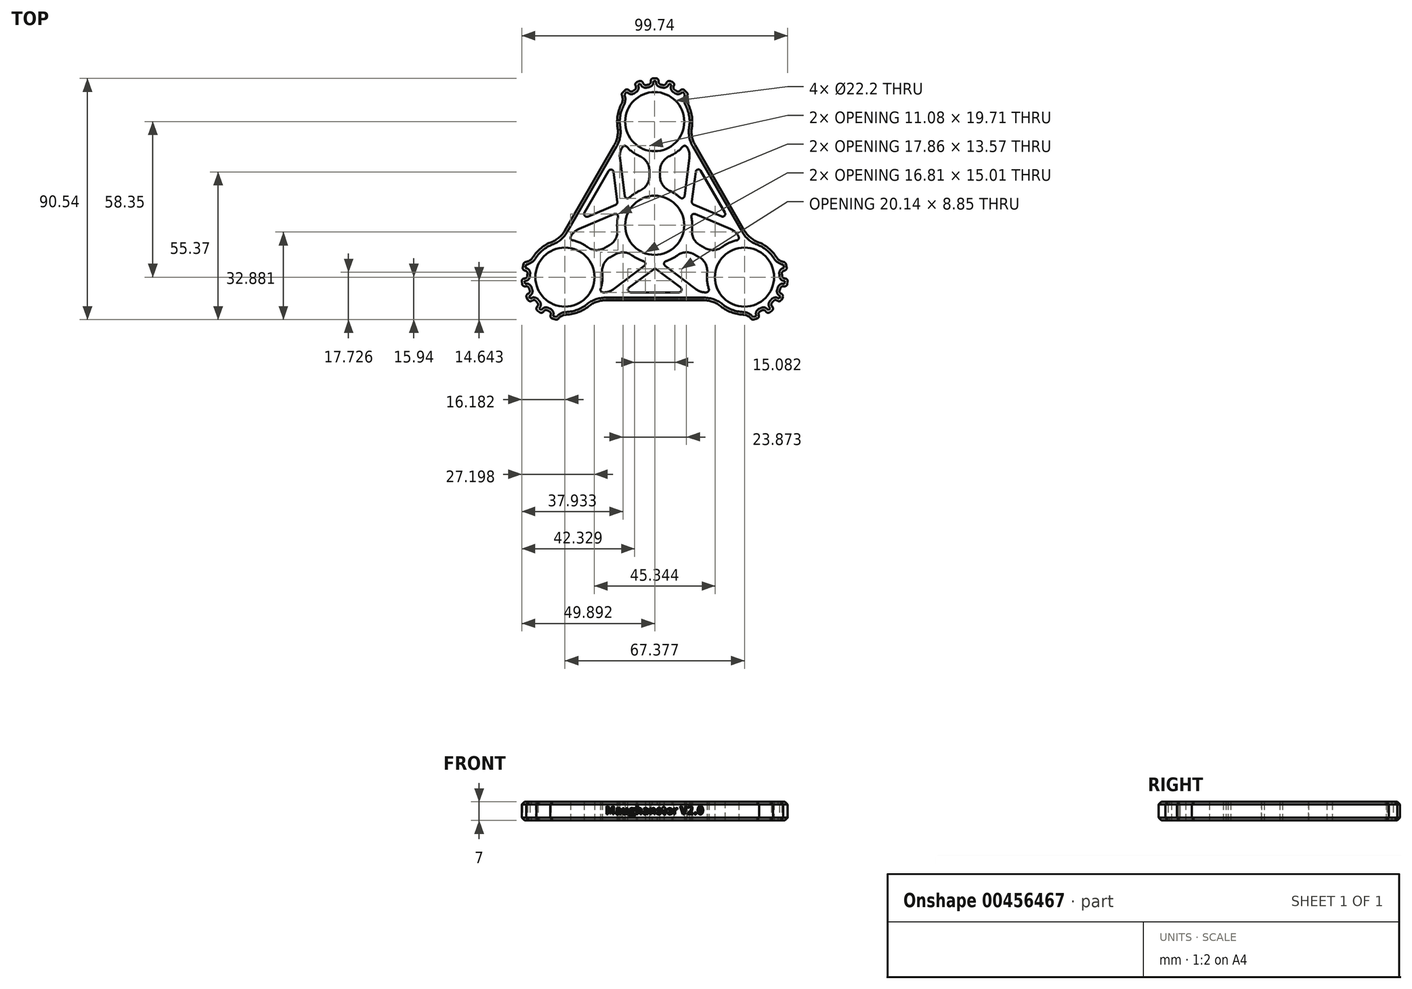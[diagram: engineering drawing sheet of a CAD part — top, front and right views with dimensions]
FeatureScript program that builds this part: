
annotation { "Feature Type Name" : "Feature", "Feature Type Description" : "" }
export const myFeature = defineFeature(function(context is Context, id is Id, definition is map)
    precondition{}
    {
        {
            var Q0;
            Q0=qCreatedBy(makeId("Top.planeOp"),FACE);
            var sketch = newSketch(context, id + "F0", { "sketchPlane" : qUnion([Q0])});
            skCircle(sketch, "E0", {"center": v(0, 0) * mm, "radius": 11.1 * mm});
            skArc(sketch, "E1.0", {"start": v(-2, 13.96) * mm, "mid": v(-6.94, 12.27) * mm, "end": v(-10.94, 8.9) * mm});
            skCircle(sketch, "E2", {"center": v(0, 38.9) * mm, "radius": 11.1 * mm});
            skArc(sketch, "E3.0", {"start": v(-10.97, 47.75) * mm, "mid": v(-13.94, 41) * mm, "end": v(-13.1, 33.66) * mm});
            skLineSegment(sketch, "E4", {"start": v(0, 11.1) * mm, "end": v(0, 27.8) * mm, "construction": true});
            skLineSegment(sketch, "E5.0", {"start": v(2, 13.96) * mm, "end": v(2, 24.94) * mm});
            skLineSegment(sketch, "E6.0", {"start": v(-2, 13.96) * mm, "end": v(-2, 24.94) * mm});
            skLineSegment(sketch, "E7", {"start": v(0, 53) * mm, "end": v(0, 55) * mm, "construction": true});
            skLineSegment(sketch, "E8.0", {"start": v(1.5, 52.92) * mm, "end": v(1.5, 55.15) * mm});
            skLineSegment(sketch, "E9.0", {"start": v(-1.5, 52.92) * mm, "end": v(-1.5, 55.15) * mm});
            skLineSegment(sketch, "E10", {"start": v(-1.5, 55.15) * mm, "end": v(1.5, 55.15) * mm});
            skLineSegment(sketch, "E11.1.0", {"start": v(4.83, 54.49) * mm, "end": v(7.6, 53.34) * mm});
            skLineSegment(sketch, "E11.1.1", {"start": v(3.98, 52.43) * mm, "end": v(4.83, 54.49) * mm});
            skLineSegment(sketch, "E11.1.2", {"start": v(6.75, 51.28) * mm, "end": v(7.6, 53.34) * mm});
            skLineSegment(sketch, "E11.2.0", {"start": v(10.43, 51.45) * mm, "end": v(12.55, 49.33) * mm});
            skLineSegment(sketch, "E11.2.1", {"start": v(8.85, 49.87) * mm, "end": v(10.43, 51.45) * mm});
            skLineSegment(sketch, "E11.2.2", {"start": v(10.97, 47.75) * mm, "end": v(12.55, 49.33) * mm});
            skLineSegment(sketch, "E11.anchor1", {"start": v(0, 38.9) * mm, "end": v(-1.5, 55.15) * mm, "construction": true});
            skLineSegment(sketch, "E11.anchor2", {"start": v(0, 38.9) * mm, "end": v(10.43, 51.45) * mm, "construction": true});
            skLineSegment(sketch, "E12.MirrorCS", {"start": v(-4.83, 54.49) * mm, "end": v(-7.6, 53.34) * mm});
            skLineSegment(sketch, "E13.MirrorCS", {"start": v(-3.98, 52.43) * mm, "end": v(-4.83, 54.49) * mm});
            skLineSegment(sketch, "E14.MirrorCS", {"start": v(-6.75, 51.28) * mm, "end": v(-7.6, 53.34) * mm});
            skLineSegment(sketch, "E15.MirrorCS", {"start": v(-8.85, 49.87) * mm, "end": v(-10.43, 51.45) * mm});
            skLineSegment(sketch, "E16.MirrorCS", {"start": v(-10.43, 51.45) * mm, "end": v(-12.55, 49.33) * mm});
            skLineSegment(sketch, "E17.MirrorCS", {"start": v(-10.97, 47.75) * mm, "end": v(-12.55, 49.33) * mm});
            skArc(sketch, "E18.trimOffspring", {"start": v(-6.75, 51.28) * mm, "mid": v(-7.83, 50.62) * mm, "end": v(-8.85, 49.87) * mm});
            skArc(sketch, "E19.trimOffspring", {"start": v(-1.3, 52.94) * mm, "mid": v(-2.65, 52.75) * mm, "end": v(-3.98, 52.43) * mm});
            skArc(sketch, "E20.trimOffspring", {"start": v(3.98, 52.43) * mm, "mid": v(2.75, 52.73) * mm, "end": v(1.5, 52.92) * mm});
            skArc(sketch, "E21.trimOffspring", {"start": v(9.01, 49.74) * mm, "mid": v(7.92, 50.57) * mm, "end": v(6.75, 51.28) * mm});
            skArc(sketch, "E22.trimOffspring", {"start": v(2, 24.94) * mm, "mid": v(7.27, 26.82) * mm, "end": v(11.4, 30.6) * mm});
            skLineSegment(sketch, "E23.1.0", {"start": v(-33.69, -19.45) * mm, "end": v(-47.01, -28.87) * mm, "construction": true});
            skPoint(sketch, "E23.1.1", {"position": v(-33.69, -19.45) * mm});
            skCircle(sketch, "E23.1.2", {"center": v(-33.69, -19.45) * mm, "radius": 11.1 * mm});
            skLineSegment(sketch, "E23.1.3", {"start": v(-9.61, -5.55) * mm, "end": v(-24.08, -13.9) * mm, "construction": true});
            skArc(sketch, "E23.1.4", {"start": v(-35.87, -33.38) * mm, "mid": v(-28.53, -32.57) * mm, "end": v(-22.6, -28.17) * mm});
            skLineSegment(sketch, "E23.1.5", {"start": v(-13.09, -5.25) * mm, "end": v(-22.6, -10.74) * mm});
            skLineSegment(sketch, "E23.1.6", {"start": v(-11.09, -8.71) * mm, "end": v(-20.6, -14.2) * mm});
            skLineSegment(sketch, "E23.1.7", {"start": v(-33.69, -19.45) * mm, "end": v(-49.77, -16.7) * mm, "construction": true});
            skArc(sketch, "E23.1.8", {"start": v(-22.6, -10.74) * mm, "mid": v(-26.86, -7.11) * mm, "end": v(-32.2, -5.43) * mm});
            skLineSegment(sketch, "E23.1.9", {"start": v(-41.03, -31.49) * mm, "end": v(-42.4, -33.26) * mm});
            skLineSegment(sketch, "E23.1.10", {"start": v(-35.87, -33.38) * mm, "end": v(-36.45, -35.53) * mm});
            skLineSegment(sketch, "E23.1.11", {"start": v(-49.77, -16.7) * mm, "end": v(-49, -13.8) * mm});
            skLineSegment(sketch, "E23.1.12", {"start": v(-47.78, -19.8) * mm, "end": v(-50, -20.08) * mm});
            skArc(sketch, "E23.1.13", {"start": v(-47.59, -17.07) * mm, "mid": v(-47.75, -18.43) * mm, "end": v(-47.78, -19.8) * mm});
            skLineSegment(sketch, "E23.1.14", {"start": v(-44.77, -31.43) * mm, "end": v(-42.4, -33.26) * mm});
            skLineSegment(sketch, "E23.1.15", {"start": v(-45.9, -26.5) * mm, "end": v(-47.63, -27.5) * mm, "construction": true});
            skLineSegment(sketch, "E23.1.16", {"start": v(-46.58, -25.16) * mm, "end": v(-48.51, -26.28) * mm});
            skLineSegment(sketch, "E23.1.17", {"start": v(-47.01, -28.87) * mm, "end": v(-48.51, -26.28) * mm});
            skLineSegment(sketch, "E23.1.18", {"start": v(-45.08, -27.76) * mm, "end": v(-47.01, -28.87) * mm});
            skLineSegment(sketch, "E23.1.19", {"start": v(-49.6, -23.06) * mm, "end": v(-50, -20.08) * mm});
            skLineSegment(sketch, "E23.1.20", {"start": v(-47.4, -22.77) * mm, "end": v(-49.6, -23.06) * mm});
            skArc(sketch, "E23.1.21", {"start": v(-47.4, -22.77) * mm, "mid": v(-47.04, -23.98) * mm, "end": v(-46.58, -25.16) * mm});
            skArc(sketch, "E23.1.22", {"start": v(-41.03, -31.49) * mm, "mid": v(-39.92, -32.1) * mm, "end": v(-38.77, -32.6) * mm});
            skLineSegment(sketch, "E23.1.23", {"start": v(-39.34, -34.76) * mm, "end": v(-36.45, -35.53) * mm});
            skLineSegment(sketch, "E23.1.24", {"start": v(-43.41, -29.66) * mm, "end": v(-44.77, -31.43) * mm});
            skLineSegment(sketch, "E23.1.25", {"start": v(-46.84, -14.37) * mm, "end": v(-49, -13.8) * mm});
            skArc(sketch, "E23.1.26", {"start": v(-45.2, -27.6) * mm, "mid": v(-44.36, -28.67) * mm, "end": v(-43.41, -29.66) * mm});
            skLineSegment(sketch, "E23.1.27", {"start": v(-38.77, -32.6) * mm, "end": v(-39.34, -34.76) * mm});
            skLineSegment(sketch, "E23.1.28", {"start": v(-47.62, -17.27) * mm, "end": v(-49.77, -16.7) * mm});
            skLineSegment(sketch, "E23.2.0", {"start": v(33.69, -19.45) * mm, "end": v(48.51, -26.28) * mm, "construction": true});
            skPoint(sketch, "E23.2.1", {"position": v(33.69, -19.45) * mm});
            skCircle(sketch, "E23.2.2", {"center": v(33.69, -19.45) * mm, "radius": 11.1 * mm});
            skLineSegment(sketch, "E23.2.3", {"start": v(9.61, -5.55) * mm, "end": v(24.08, -13.9) * mm, "construction": true});
            skArc(sketch, "E23.2.4", {"start": v(46.84, -14.37) * mm, "mid": v(42.48, -8.42) * mm, "end": v(35.7, -5.5) * mm});
            skLineSegment(sketch, "E23.2.5", {"start": v(11.09, -8.71) * mm, "end": v(20.6, -14.2) * mm});
            skLineSegment(sketch, "E23.2.6", {"start": v(13.09, -5.25) * mm, "end": v(22.6, -10.74) * mm});
            skLineSegment(sketch, "E23.2.7", {"start": v(33.69, -19.45) * mm, "end": v(39.34, -34.76) * mm, "construction": true});
            skArc(sketch, "E23.2.8", {"start": v(20.6, -14.2) * mm, "mid": v(19.6, -19.7) * mm, "end": v(20.8, -25.17) * mm});
            skLineSegment(sketch, "E23.2.9", {"start": v(47.78, -19.8) * mm, "end": v(50, -20.08) * mm});
            skLineSegment(sketch, "E23.2.10", {"start": v(46.84, -14.37) * mm, "end": v(49, -13.8) * mm});
            skLineSegment(sketch, "E23.2.11", {"start": v(39.34, -34.76) * mm, "end": v(36.45, -35.53) * mm});
            skLineSegment(sketch, "E23.2.12", {"start": v(41.03, -31.49) * mm, "end": v(42.4, -33.26) * mm});
            skArc(sketch, "E23.2.13", {"start": v(38.57, -32.68) * mm, "mid": v(39.83, -32.14) * mm, "end": v(41.03, -31.49) * mm});
            skLineSegment(sketch, "E23.2.14", {"start": v(49.6, -23.06) * mm, "end": v(50, -20.08) * mm});
            skLineSegment(sketch, "E23.2.15", {"start": v(45.9, -26.5) * mm, "end": v(47.63, -27.5) * mm, "construction": true});
            skLineSegment(sketch, "E23.2.16", {"start": v(45.08, -27.76) * mm, "end": v(47.01, -28.87) * mm});
            skLineSegment(sketch, "E23.2.17", {"start": v(48.51, -26.28) * mm, "end": v(47.01, -28.87) * mm});
            skLineSegment(sketch, "E23.2.18", {"start": v(46.58, -25.16) * mm, "end": v(48.51, -26.28) * mm});
            skLineSegment(sketch, "E23.2.19", {"start": v(44.77, -31.43) * mm, "end": v(42.4, -33.26) * mm});
            skLineSegment(sketch, "E23.2.20", {"start": v(43.41, -29.66) * mm, "end": v(44.77, -31.43) * mm});
            skArc(sketch, "E23.2.21", {"start": v(43.41, -29.66) * mm, "mid": v(44.29, -28.75) * mm, "end": v(45.08, -27.76) * mm});
            skArc(sketch, "E23.2.22", {"start": v(47.78, -19.8) * mm, "mid": v(47.76, -18.53) * mm, "end": v(47.62, -17.27) * mm});
            skLineSegment(sketch, "E23.2.23", {"start": v(49.77, -16.7) * mm, "end": v(49, -13.8) * mm});
            skLineSegment(sketch, "E23.2.24", {"start": v(47.4, -22.77) * mm, "end": v(49.6, -23.06) * mm});
            skLineSegment(sketch, "E23.2.25", {"start": v(35.87, -33.38) * mm, "end": v(36.45, -35.53) * mm});
            skArc(sketch, "E23.2.26", {"start": v(46.5, -25.35) * mm, "mid": v(47, -24.08) * mm, "end": v(47.4, -22.77) * mm});
            skLineSegment(sketch, "E23.2.27", {"start": v(47.62, -17.27) * mm, "end": v(49.77, -16.7) * mm});
            skLineSegment(sketch, "E23.2.28", {"start": v(38.77, -32.6) * mm, "end": v(39.34, -34.76) * mm});
            skArc(sketch, "E24.trimOffspring", {"start": v(13.09, -5.25) * mm, "mid": v(14.1, -0.12) * mm, "end": v(13.18, 5.02) * mm});
            skArc(sketch, "E25.trimOffspring", {"start": v(-11.09, -8.71) * mm, "mid": v(-7.15, -12.15) * mm, "end": v(-2.24, -13.92) * mm});
            skLineSegment(sketch, "E26", {"start": v(-13.1, 33.66) * mm, "end": v(-35.7, -5.5) * mm});
            skLineSegment(sketch, "E27.0", {"start": v(-11.4, 30.6) * mm, "end": v(-13.3, 27.31) * mm});
            skArc(sketch, "E28.trimOffspring", {"start": v(-11.4, 30.6) * mm, "mid": v(-7.27, 26.82) * mm, "end": v(-2, 24.94) * mm});
            skArc(sketch, "E29.trimOffspring", {"start": v(-35.7, -5.5) * mm, "mid": v(-42.48, -8.42) * mm, "end": v(-46.84, -14.37) * mm});
            skLineSegment(sketch, "E30", {"start": v(-12.21, 7.05) * mm, "end": v(-29.06, 0) * mm, "construction": true});
            skLineSegment(sketch, "E31", {"start": v(-12.21, 7.05) * mm, "end": v(-21.8, 12.59) * mm, "construction": true});
            skLineSegment(sketch, "E32.0", {"start": v(-13.97, 7.94) * mm, "end": v(-27.83, 2.14) * mm});
            skLineSegment(sketch, "E33.0", {"start": v(-13.18, 5.02) * mm, "end": v(-30.3, -2.14) * mm});
            skLineSegment(sketch, "E34.trimOffspring", {"start": v(-30.3, -2.14) * mm, "end": v(-32.2, -5.43) * mm});
            skArc(sketch, "E35.trimOffspring", {"start": v(-13.18, 5.02) * mm, "mid": v(-14.1, -0.12) * mm, "end": v(-13.09, -5.25) * mm});
            skLineSegment(sketch, "E36.MirrorCS", {"start": v(-10.94, 8.9) * mm, "end": v(-13.3, 27.31) * mm});
            skLineSegment(sketch, "E37.trimOffspring", {"start": v(-15.77, 23.03) * mm, "end": v(-27.83, 2.14) * mm});
            skPoint(sketch, "E38.orphan", {"position": v(-10.53, 9.38) * mm});
            skLineSegment(sketch, "E39.trimOffspring", {"start": v(-13.97, 7.94) * mm, "end": v(-15.77, 23.03) * mm});
            skPoint(sketch, "E40.MirrorCS.start.orphan", {"position": v(-13.39, 4.43) * mm});
            skLineSegment(sketch, "E41.1.0", {"start": v(-22.6, -28.17) * mm, "end": v(22.6, -28.17) * mm});
            skLineSegment(sketch, "E41.1.1", {"start": v(0.11, -16.07) * mm, "end": v(-12.06, -25.17) * mm});
            skLineSegment(sketch, "E41.1.2", {"start": v(0, -14.1) * mm, "end": v(0, -25.17) * mm, "construction": true});
            skLineSegment(sketch, "E41.1.3", {"start": v(-12.06, -25.17) * mm, "end": v(12.06, -25.17) * mm});
            skLineSegment(sketch, "E41.1.4", {"start": v(-2.24, -13.92) * mm, "end": v(-17, -25.17) * mm});
            skLineSegment(sketch, "E41.1.5", {"start": v(17, -25.17) * mm, "end": v(20.8, -25.17) * mm});
            skLineSegment(sketch, "E41.1.6", {"start": v(2.24, -13.92) * mm, "end": v(17, -25.17) * mm});
            skLineSegment(sketch, "E41.1.7", {"start": v(0.11, -16.07) * mm, "end": v(12.06, -25.17) * mm});
            skLineSegment(sketch, "E41.1.8", {"start": v(0, -14.1) * mm, "end": v(14.53, -25.17) * mm, "construction": true});
            skLineSegment(sketch, "E41.1.9", {"start": v(-20.8, -25.17) * mm, "end": v(-17, -25.17) * mm});
            skLineSegment(sketch, "E41.2.0", {"start": v(35.7, -5.5) * mm, "end": v(13.1, 33.66) * mm});
            skLineSegment(sketch, "E41.2.1", {"start": v(13.86, 8.13) * mm, "end": v(27.83, 2.14) * mm});
            skLineSegment(sketch, "E41.2.2", {"start": v(12.21, 7.05) * mm, "end": v(21.8, 12.59) * mm, "construction": true});
            skLineSegment(sketch, "E41.2.3", {"start": v(27.83, 2.14) * mm, "end": v(15.77, 23.03) * mm});
            skLineSegment(sketch, "E41.2.4", {"start": v(13.18, 5.02) * mm, "end": v(30.3, -2.14) * mm});
            skLineSegment(sketch, "E41.2.5", {"start": v(13.3, 27.31) * mm, "end": v(11.4, 30.6) * mm});
            skLineSegment(sketch, "E41.2.6", {"start": v(10.94, 8.9) * mm, "end": v(13.3, 27.31) * mm});
            skLineSegment(sketch, "E41.2.7", {"start": v(13.86, 8.13) * mm, "end": v(15.77, 23.03) * mm});
            skLineSegment(sketch, "E41.2.8", {"start": v(12.21, 7.05) * mm, "end": v(14.53, 25.17) * mm, "construction": true});
            skLineSegment(sketch, "E41.2.9", {"start": v(32.2, -5.43) * mm, "end": v(30.3, -2.14) * mm});
            skArc(sketch, "E42.trimOffspring", {"start": v(13.1, 33.66) * mm, "mid": v(13.94, 41) * mm, "end": v(10.97, 47.75) * mm});
            skArc(sketch, "E43.trimOffspring", {"start": v(32.2, -5.43) * mm, "mid": v(26.86, -7.11) * mm, "end": v(22.6, -10.74) * mm});
            skArc(sketch, "E44.trimOffspring", {"start": v(10.94, 8.9) * mm, "mid": v(6.94, 12.27) * mm, "end": v(2, 13.96) * mm});
            skArc(sketch, "E45.trimOffspring", {"start": v(2.24, -13.92) * mm, "mid": v(7.15, -12.15) * mm, "end": v(11.09, -8.71) * mm});
            skArc(sketch, "E46.trimOffspring", {"start": v(22.6, -28.17) * mm, "mid": v(28.53, -32.57) * mm, "end": v(35.87, -33.38) * mm});
            skArc(sketch, "E47.trimOffspring", {"start": v(-20.8, -25.17) * mm, "mid": v(-19.6, -19.7) * mm, "end": v(-20.6, -14.2) * mm});
            skSolve(sketch);
        }
        {
            var Q0;
            Q0 = qSketchRegion(id + "F0", true);
            extrude(context, id + "F1", {"entities" : qUnion([Q0]), "depth" : 7 * mm});
        }
        {
            var Q0;
            Q0=makeQuery(id+"F1.opExtrude","SWEPT_EDGE",EDGE,{"disambiguationData":[OSD([sQuery(id+"F0.wireOp",EDGE,"E1.0"),sQuery(id+"F0.wireOp",EDGE,"E6.0")])]});
            var Q1;
            Q1=makeQuery(id+"F1.opExtrude","SWEPT_EDGE",EDGE,{"disambiguationData":[OSD([sQuery(id+"F0.wireOp",EDGE,"E5.0"),sQuery(id+"F0.wireOp",EDGE,"E44.trimOffspring")])]});
            var Q2;
            Q2=makeQuery(id+"F1.opExtrude","SWEPT_EDGE",EDGE,{"disambiguationData":[OSD([sQuery(id+"F0.wireOp",EDGE,"E5.0"),sQuery(id+"F0.wireOp",EDGE,"E22.trimOffspring")])]});
            var Q3;
            Q3=makeQuery(id+"F1.opExtrude","SWEPT_EDGE",EDGE,{"disambiguationData":[OSD([sQuery(id+"F0.wireOp",EDGE,"E6.0"),sQuery(id+"F0.wireOp",EDGE,"E28.trimOffspring")])]});
            var Q4;
            Q4=makeQuery(id+"F1.opExtrude","SWEPT_EDGE",EDGE,{"disambiguationData":[OSD([sQuery(id+"F0.wireOp",EDGE,"E23.1.5"),sQuery(id+"F0.wireOp",EDGE,"E35.trimOffspring")])]});
            var Q5;
            Q5=makeQuery(id+"F1.opExtrude","SWEPT_EDGE",EDGE,{"disambiguationData":[OSD([sQuery(id+"F0.wireOp",EDGE,"E23.2.5"),sQuery(id+"F0.wireOp",EDGE,"E23.2.8")])]});
            var Q6;
            Q6=makeQuery(id+"F1.opExtrude","SWEPT_EDGE",EDGE,{"disambiguationData":[OSD([sQuery(id+"F0.wireOp",EDGE,"E23.1.6"),sQuery(id+"F0.wireOp",EDGE,"E47.trimOffspring")])]});
            var Q7;
            Q7=makeQuery(id+"F1.opExtrude","SWEPT_EDGE",EDGE,{"disambiguationData":[OSD([sQuery(id+"F0.wireOp",EDGE,"E23.1.6"),sQuery(id+"F0.wireOp",EDGE,"E25.trimOffspring")])]});
            var Q8;
            Q8=makeQuery(id+"F1.opExtrude","SWEPT_EDGE",EDGE,{"disambiguationData":[OSD([sQuery(id+"F0.wireOp",EDGE,"E23.1.5"),sQuery(id+"F0.wireOp",EDGE,"E23.1.8")])]});
            var Q9;
            Q9=makeQuery(id+"F1.opExtrude","SWEPT_EDGE",EDGE,{"disambiguationData":[OSD([sQuery(id+"F0.wireOp",EDGE,"E23.2.6"),sQuery(id+"F0.wireOp",EDGE,"E43.trimOffspring")])]});
            var Q10;
            Q10=makeQuery(id+"F1.opExtrude","SWEPT_EDGE",EDGE,{"disambiguationData":[OSD([sQuery(id+"F0.wireOp",EDGE,"E23.2.5"),sQuery(id+"F0.wireOp",EDGE,"E45.trimOffspring")])]});
            var Q11;
            Q11=makeQuery(id+"F1.opExtrude","SWEPT_EDGE",EDGE,{"disambiguationData":[OSD([sQuery(id+"F0.wireOp",EDGE,"E23.2.6"),sQuery(id+"F0.wireOp",EDGE,"E24.trimOffspring")])]});
            var Q12;
            Q12=makeQuery(id+"F1.opExtrude","SWEPT_EDGE",EDGE,{"disambiguationData":[OSD([sQuery(id+"F0.wireOp",EDGE,"E33.0"),sQuery(id+"F0.wireOp",EDGE,"E34.trimOffspring")])]});
            var Q13;
            Q13=makeQuery(id+"F1.opExtrude","SWEPT_EDGE",EDGE,{"disambiguationData":[OSD([sQuery(id+"F0.wireOp",EDGE,"E41.1.4"),sQuery(id+"F0.wireOp",EDGE,"E41.1.9")])]});
            var Q14;
            Q14=makeQuery(id+"F1.opExtrude","SWEPT_EDGE",EDGE,{"disambiguationData":[OSD([sQuery(id+"F0.wireOp",EDGE,"E41.1.5"),sQuery(id+"F0.wireOp",EDGE,"E41.1.6")])]});
            var Q15;
            Q15=makeQuery(id+"F1.opExtrude","SWEPT_EDGE",EDGE,{"disambiguationData":[OSD([sQuery(id+"F0.wireOp",EDGE,"E41.2.5"),sQuery(id+"F0.wireOp",EDGE,"E41.2.6")])]});
            var Q16;
            Q16=makeQuery(id+"F1.opExtrude","SWEPT_EDGE",EDGE,{"disambiguationData":[OSD([sQuery(id+"F0.wireOp",EDGE,"E41.2.4"),sQuery(id+"F0.wireOp",EDGE,"E41.2.9")])]});
            var Q17;
            Q17=makeQuery(id+"F1.opExtrude","SWEPT_EDGE",EDGE,{"disambiguationData":[OSD([sQuery(id+"F0.wireOp",EDGE,"E27.0"),sQuery(id+"F0.wireOp",EDGE,"E36.MirrorCS")])]});
            fillet(context, id + "F2", {"entities" : qUnion([Q0, Q1, Q2, Q3, Q4, Q5, Q6, Q7, Q8, Q9, Q10, Q11, Q12, Q13, Q14, Q15, Q16, Q17]), "radius" : 6 * mm, "tangentPropagation" : true, "allowEdgeOverflow" : false});
        }
        {
            var Q0;
            Q0=makeQuery(id+"F1.opExtrude","SWEPT_EDGE",EDGE,{"disambiguationData":[OSD([sQuery(id+"F0.wireOp",EDGE,"E1.0"),sQuery(id+"F0.wireOp",EDGE,"E36.MirrorCS")])]});
            var Q1;
            Q1=makeQuery(id+"F1.opExtrude","SWEPT_EDGE",EDGE,{"disambiguationData":[OSD([sQuery(id+"F0.wireOp",EDGE,"E33.0"),sQuery(id+"F0.wireOp",EDGE,"E35.trimOffspring")])]});
            var Q2;
            Q2=makeQuery(id+"F1.opExtrude","SWEPT_EDGE",EDGE,{"disambiguationData":[OSD([sQuery(id+"F0.wireOp",EDGE,"E25.trimOffspring"),sQuery(id+"F0.wireOp",EDGE,"E41.1.4")])]});
            var Q3;
            Q3=makeQuery(id+"F1.opExtrude","SWEPT_EDGE",EDGE,{"disambiguationData":[OSD([sQuery(id+"F0.wireOp",EDGE,"E41.1.6"),sQuery(id+"F0.wireOp",EDGE,"E45.trimOffspring")])]});
            var Q4;
            Q4=makeQuery(id+"F1.opExtrude","SWEPT_EDGE",EDGE,{"disambiguationData":[OSD([sQuery(id+"F0.wireOp",EDGE,"E24.trimOffspring"),sQuery(id+"F0.wireOp",EDGE,"E41.2.4")])]});
            var Q5;
            Q5=makeQuery(id+"F1.opExtrude","SWEPT_EDGE",EDGE,{"disambiguationData":[OSD([sQuery(id+"F0.wireOp",EDGE,"E41.2.6"),sQuery(id+"F0.wireOp",EDGE,"E44.trimOffspring")])]});
            var Q6;
            Q6=makeQuery(id+"F1.opExtrude","SWEPT_EDGE",EDGE,{"disambiguationData":[OSD([sQuery(id+"F0.wireOp",EDGE,"E41.2.9"),sQuery(id+"F0.wireOp",EDGE,"E43.trimOffspring")])]});
            var Q7;
            Q7=makeQuery(id+"F1.opExtrude","SWEPT_EDGE",EDGE,{"disambiguationData":[OSD([sQuery(id+"F0.wireOp",EDGE,"E23.2.8"),sQuery(id+"F0.wireOp",EDGE,"E41.1.5")])]});
            var Q8;
            Q8=makeQuery(id+"F1.opExtrude","SWEPT_EDGE",EDGE,{"disambiguationData":[OSD([sQuery(id+"F0.wireOp",EDGE,"E41.1.9"),sQuery(id+"F0.wireOp",EDGE,"E47.trimOffspring")])]});
            var Q9;
            Q9=makeQuery(id+"F1.opExtrude","SWEPT_EDGE",EDGE,{"disambiguationData":[OSD([sQuery(id+"F0.wireOp",EDGE,"E23.1.8"),sQuery(id+"F0.wireOp",EDGE,"E34.trimOffspring")])]});
            var Q10;
            Q10=makeQuery(id+"F1.opExtrude","SWEPT_EDGE",EDGE,{"disambiguationData":[OSD([sQuery(id+"F0.wireOp",EDGE,"E22.trimOffspring"),sQuery(id+"F0.wireOp",EDGE,"E41.2.5")])]});
            var Q11;
            Q11=makeQuery(id+"F1.opExtrude","SWEPT_EDGE",EDGE,{"disambiguationData":[OSD([sQuery(id+"F0.wireOp",EDGE,"E27.0"),sQuery(id+"F0.wireOp",EDGE,"E28.trimOffspring")])]});
            var Q12;
            Q12=makeQuery(id+"F1.opExtrude","SWEPT_EDGE",EDGE,{"disambiguationData":[OSD([sQuery(id+"F0.wireOp",EDGE,"E37.trimOffspring"),sQuery(id+"F0.wireOp",EDGE,"E39.trimOffspring")])]});
            var Q13;
            Q13=makeQuery(id+"F1.opExtrude","SWEPT_EDGE",EDGE,{"disambiguationData":[OSD([sQuery(id+"F0.wireOp",EDGE,"E32.0"),sQuery(id+"F0.wireOp",EDGE,"E37.trimOffspring")])]});
            var Q14;
            Q14=makeQuery(id+"F1.opExtrude","SWEPT_EDGE",EDGE,{"disambiguationData":[OSD([sQuery(id+"F0.wireOp",EDGE,"E41.2.1"),sQuery(id+"F0.wireOp",EDGE,"E41.2.3")])]});
            var Q15;
            Q15=makeQuery(id+"F1.opExtrude","SWEPT_EDGE",EDGE,{"disambiguationData":[OSD([sQuery(id+"F0.wireOp",EDGE,"E41.2.3"),sQuery(id+"F0.wireOp",EDGE,"E41.2.7")])]});
            var Q16;
            Q16=makeQuery(id+"F1.opExtrude","SWEPT_EDGE",EDGE,{"disambiguationData":[OSD([sQuery(id+"F0.wireOp",EDGE,"E41.1.3"),sQuery(id+"F0.wireOp",EDGE,"E41.1.7")])]});
            var Q17;
            Q17=makeQuery(id+"F1.opExtrude","SWEPT_EDGE",EDGE,{"disambiguationData":[OSD([sQuery(id+"F0.wireOp",EDGE,"E41.1.1"),sQuery(id+"F0.wireOp",EDGE,"E41.1.3")])]});
            var Q18;
            Q18=makeQuery(id+"F1.opExtrude","SWEPT_EDGE",EDGE,{"disambiguationData":[OSD([sQuery(id+"F0.wireOp",EDGE,"E32.0"),sQuery(id+"F0.wireOp",EDGE,"E39.trimOffspring")])]});
            var Q19;
            Q19=makeQuery(id+"F1.opExtrude","SWEPT_EDGE",EDGE,{"disambiguationData":[OSD([sQuery(id+"F0.wireOp",EDGE,"E41.1.1"),sQuery(id+"F0.wireOp",EDGE,"E41.1.7")])]});
            var Q20;
            Q20=makeQuery(id+"F1.opExtrude","SWEPT_EDGE",EDGE,{"disambiguationData":[OSD([sQuery(id+"F0.wireOp",EDGE,"E41.2.1"),sQuery(id+"F0.wireOp",EDGE,"E41.2.7")])]});
            fillet(context, id + "F3", {"entities" : qUnion([Q0, Q1, Q2, Q3, Q4, Q5, Q6, Q7, Q8, Q9, Q10, Q11, Q12, Q13, Q14, Q15, Q16, Q17, Q18, Q19, Q20]), "radius" : 1 * mm, "tangentPropagation" : true, "allowEdgeOverflow" : false});
        }
        {
            var Q0;
            Q0=makeQuery(id+"F1.opExtrude","SWEPT_EDGE",EDGE,{"disambiguationData":[OSD([sQuery(id+"F0.wireOp",EDGE,"E3.0"),sQuery(id+"F0.wireOp",EDGE,"E26")])]});
            var Q1;
            Q1=makeQuery(id+"F1.opExtrude","SWEPT_EDGE",EDGE,{"disambiguationData":[OSD([sQuery(id+"F0.wireOp",EDGE,"E41.2.0"),sQuery(id+"F0.wireOp",EDGE,"E42.trimOffspring")])]});
            var Q2;
            Q2=makeQuery(id+"F1.opExtrude","SWEPT_EDGE",EDGE,{"disambiguationData":[OSD([sQuery(id+"F0.wireOp",EDGE,"E26"),sQuery(id+"F0.wireOp",EDGE,"E29.trimOffspring")])]});
            var Q3;
            Q3=makeQuery(id+"F1.opExtrude","SWEPT_EDGE",EDGE,{"disambiguationData":[OSD([sQuery(id+"F0.wireOp",EDGE,"E23.1.4"),sQuery(id+"F0.wireOp",EDGE,"E41.1.0")])]});
            var Q4;
            Q4=makeQuery(id+"F1.opExtrude","SWEPT_EDGE",EDGE,{"disambiguationData":[OSD([sQuery(id+"F0.wireOp",EDGE,"E41.1.0"),sQuery(id+"F0.wireOp",EDGE,"E46.trimOffspring")])]});
            var Q5;
            Q5=makeQuery(id+"F1.opExtrude","SWEPT_EDGE",EDGE,{"disambiguationData":[OSD([sQuery(id+"F0.wireOp",EDGE,"E23.2.4"),sQuery(id+"F0.wireOp",EDGE,"E41.2.0")])]});
            fillet(context, id + "F4", {"entities" : qUnion([Q0, Q1, Q2, Q3, Q4, Q5]), "radius" : 10 * mm, "tangentPropagation" : true, "allowEdgeOverflow" : false});
        }
        {
            var Q0;
            Q0=makeQuery(id+"F1.opExtrude","SWEPT_EDGE",EDGE,{"disambiguationData":[OSD([sQuery(id+"F0.wireOp",EDGE,"E3.0"),sQuery(id+"F0.wireOp",EDGE,"E17.MirrorCS")])]});
            var Q1;
            Q1=makeQuery(id+"F1.opExtrude","SWEPT_EDGE",EDGE,{"disambiguationData":[OSD([sQuery(id+"F0.wireOp",EDGE,"E11.2.2"),sQuery(id+"F0.wireOp",EDGE,"E42.trimOffspring")])]});
            var Q2;
            Q2=makeQuery(id+"F1.opExtrude","SWEPT_EDGE",EDGE,{"disambiguationData":[OSD([sQuery(id+"F0.wireOp",EDGE,"E23.1.25"),sQuery(id+"F0.wireOp",EDGE,"E29.trimOffspring")])]});
            var Q3;
            Q3=makeQuery(id+"F1.opExtrude","SWEPT_EDGE",EDGE,{"disambiguationData":[OSD([sQuery(id+"F0.wireOp",EDGE,"E23.1.4"),sQuery(id+"F0.wireOp",EDGE,"E23.1.10")])]});
            var Q4;
            Q4=makeQuery(id+"F1.opExtrude","SWEPT_EDGE",EDGE,{"disambiguationData":[OSD([sQuery(id+"F0.wireOp",EDGE,"E23.2.25"),sQuery(id+"F0.wireOp",EDGE,"E46.trimOffspring")])]});
            var Q5;
            Q5=makeQuery(id+"F1.opExtrude","SWEPT_EDGE",EDGE,{"disambiguationData":[OSD([sQuery(id+"F0.wireOp",EDGE,"E23.2.4"),sQuery(id+"F0.wireOp",EDGE,"E23.2.10")])]});
            fillet(context, id + "F5", {"entities" : qUnion([Q0, Q1, Q2, Q3, Q4, Q5]), "radius" : 4 * mm, "tangentPropagation" : true, "allowEdgeOverflow" : false});
        }
        {
            var Q0;
            Q0=makeQuery(id+"F1.opExtrude","SWEPT_EDGE",EDGE,{"disambiguationData":[OSD([sQuery(id+"F0.wireOp",EDGE,"E15.MirrorCS"),sQuery(id+"F0.wireOp",EDGE,"E18.trimOffspring")])]});
            var Q1;
            Q1=makeQuery(id+"F1.opExtrude","SWEPT_EDGE",EDGE,{"disambiguationData":[OSD([sQuery(id+"F0.wireOp",EDGE,"E14.MirrorCS"),sQuery(id+"F0.wireOp",EDGE,"E18.trimOffspring")])]});
            var Q2;
            Q2=makeQuery(id+"F1.opExtrude","SWEPT_EDGE",EDGE,{"disambiguationData":[OSD([sQuery(id+"F0.wireOp",EDGE,"E13.MirrorCS"),sQuery(id+"F0.wireOp",EDGE,"E19.trimOffspring")])]});
            var Q3;
            Q3=makeQuery(id+"F1.opExtrude","SWEPT_EDGE",EDGE,{"disambiguationData":[OSD([sQuery(id+"F0.wireOp",EDGE,"E9.0"),sQuery(id+"F0.wireOp",EDGE,"E19.trimOffspring")])]});
            var Q4;
            Q4=makeQuery(id+"F1.opExtrude","SWEPT_EDGE",EDGE,{"disambiguationData":[OSD([sQuery(id+"F0.wireOp",EDGE,"E8.0"),sQuery(id+"F0.wireOp",EDGE,"E20.trimOffspring")])]});
            var Q5;
            Q5=makeQuery(id+"F1.opExtrude","SWEPT_EDGE",EDGE,{"disambiguationData":[OSD([sQuery(id+"F0.wireOp",EDGE,"E11.1.2"),sQuery(id+"F0.wireOp",EDGE,"E21.trimOffspring")])]});
            var Q6;
            Q6=makeQuery(id+"F1.opExtrude","SWEPT_EDGE",EDGE,{"disambiguationData":[OSD([sQuery(id+"F0.wireOp",EDGE,"E11.1.1"),sQuery(id+"F0.wireOp",EDGE,"E20.trimOffspring")])]});
            var Q7;
            Q7=makeQuery(id+"F1.opExtrude","SWEPT_EDGE",EDGE,{"disambiguationData":[OSD([sQuery(id+"F0.wireOp",EDGE,"E11.2.1"),sQuery(id+"F0.wireOp",EDGE,"E21.trimOffspring")])]});
            var Q8;
            Q8=makeQuery(id+"F1.opExtrude","SWEPT_EDGE",EDGE,{"disambiguationData":[OSD([sQuery(id+"F0.wireOp",EDGE,"E23.1.13"),sQuery(id+"F0.wireOp",EDGE,"E23.1.28")])]});
            var Q9;
            Q9=makeQuery(id+"F1.opExtrude","SWEPT_EDGE",EDGE,{"disambiguationData":[OSD([sQuery(id+"F0.wireOp",EDGE,"E23.1.20"),sQuery(id+"F0.wireOp",EDGE,"E23.1.21")])]});
            var Q10;
            Q10=makeQuery(id+"F1.opExtrude","SWEPT_EDGE",EDGE,{"disambiguationData":[OSD([sQuery(id+"F0.wireOp",EDGE,"E23.1.9"),sQuery(id+"F0.wireOp",EDGE,"E23.1.22")])]});
            var Q11;
            Q11=makeQuery(id+"F1.opExtrude","SWEPT_EDGE",EDGE,{"disambiguationData":[OSD([sQuery(id+"F0.wireOp",EDGE,"E23.1.18"),sQuery(id+"F0.wireOp",EDGE,"E23.1.26")])]});
            var Q12;
            Q12=makeQuery(id+"F1.opExtrude","SWEPT_EDGE",EDGE,{"disambiguationData":[OSD([sQuery(id+"F0.wireOp",EDGE,"E23.1.12"),sQuery(id+"F0.wireOp",EDGE,"E23.1.13")])]});
            var Q13;
            Q13=makeQuery(id+"F1.opExtrude","SWEPT_EDGE",EDGE,{"disambiguationData":[OSD([sQuery(id+"F0.wireOp",EDGE,"E23.1.16"),sQuery(id+"F0.wireOp",EDGE,"E23.1.21")])]});
            var Q14;
            Q14=makeQuery(id+"F1.opExtrude","SWEPT_EDGE",EDGE,{"disambiguationData":[OSD([sQuery(id+"F0.wireOp",EDGE,"E23.1.24"),sQuery(id+"F0.wireOp",EDGE,"E23.1.26")])]});
            var Q15;
            Q15=makeQuery(id+"F1.opExtrude","SWEPT_EDGE",EDGE,{"disambiguationData":[OSD([sQuery(id+"F0.wireOp",EDGE,"E23.1.22"),sQuery(id+"F0.wireOp",EDGE,"E23.1.27")])]});
            var Q16;
            Q16=makeQuery(id+"F1.opExtrude","SWEPT_EDGE",EDGE,{"disambiguationData":[OSD([sQuery(id+"F0.wireOp",EDGE,"E23.2.22"),sQuery(id+"F0.wireOp",EDGE,"E23.2.27")])]});
            var Q17;
            Q17=makeQuery(id+"F1.opExtrude","SWEPT_EDGE",EDGE,{"disambiguationData":[OSD([sQuery(id+"F0.wireOp",EDGE,"E23.2.24"),sQuery(id+"F0.wireOp",EDGE,"E23.2.26")])]});
            var Q18;
            Q18=makeQuery(id+"F1.opExtrude","SWEPT_EDGE",EDGE,{"disambiguationData":[OSD([sQuery(id+"F0.wireOp",EDGE,"E23.2.16"),sQuery(id+"F0.wireOp",EDGE,"E23.2.21")])]});
            var Q19;
            Q19=makeQuery(id+"F1.opExtrude","SWEPT_EDGE",EDGE,{"disambiguationData":[OSD([sQuery(id+"F0.wireOp",EDGE,"E23.2.12"),sQuery(id+"F0.wireOp",EDGE,"E23.2.13")])]});
            var Q20;
            Q20=makeQuery(id+"F1.opExtrude","SWEPT_EDGE",EDGE,{"disambiguationData":[OSD([sQuery(id+"F0.wireOp",EDGE,"E23.2.13"),sQuery(id+"F0.wireOp",EDGE,"E23.2.28")])]});
            var Q21;
            Q21=makeQuery(id+"F1.opExtrude","SWEPT_EDGE",EDGE,{"disambiguationData":[OSD([sQuery(id+"F0.wireOp",EDGE,"E23.2.20"),sQuery(id+"F0.wireOp",EDGE,"E23.2.21")])]});
            var Q22;
            Q22=makeQuery(id+"F1.opExtrude","SWEPT_EDGE",EDGE,{"disambiguationData":[OSD([sQuery(id+"F0.wireOp",EDGE,"E23.2.18"),sQuery(id+"F0.wireOp",EDGE,"E23.2.26")])]});
            var Q23;
            Q23=makeQuery(id+"F1.opExtrude","SWEPT_EDGE",EDGE,{"disambiguationData":[OSD([sQuery(id+"F0.wireOp",EDGE,"E23.2.9"),sQuery(id+"F0.wireOp",EDGE,"E23.2.22")])]});
            fillet(context, id + "F6", {"entities" : qUnion([Q0, Q1, Q2, Q3, Q4, Q5, Q6, Q7, Q8, Q9, Q10, Q11, Q12, Q13, Q14, Q15, Q16, Q17, Q18, Q19, Q20, Q21, Q22, Q23]), "radius" : 1 * mm, "tangentPropagation" : true, "allowEdgeOverflow" : false});
        }
        {
            var Q0;
            Q0=makeQuery(id+"F1.opExtrude","SWEPT_EDGE",EDGE,{"disambiguationData":[OSD([sQuery(id+"F0.wireOp",EDGE,"E12.MirrorCS"),sQuery(id+"F0.wireOp",EDGE,"E14.MirrorCS")])]});
            var Q1;
            Q1=makeQuery(id+"F1.opExtrude","SWEPT_EDGE",EDGE,{"disambiguationData":[OSD([sQuery(id+"F0.wireOp",EDGE,"E12.MirrorCS"),sQuery(id+"F0.wireOp",EDGE,"E13.MirrorCS")])]});
            var Q2;
            Q2=makeQuery(id+"F5.opFillet","BLEND_EDGE",EDGE,{"blendedFrom":[makeQuery(id+"F1.opExtrude","SWEPT_EDGE",EDGE,{"disambiguationData":[OSD([sQuery(id+"F0.wireOp",EDGE,"E3.0"),sQuery(id+"F0.wireOp",EDGE,"E17.MirrorCS")])]}),makeQuery(id+"F1.opExtrude","SWEPT_FACE",FACE,{"disambiguationData":[OSD([sQuery(id+"F0.wireOp",EDGE,"E16.MirrorCS")])]})],"blendedInto":[makeQuery(id+"F1.opExtrude","SWEPT_FACE",FACE,{"disambiguationData":[OSD([sQuery(id+"F0.wireOp",EDGE,"E16.MirrorCS")])]})]});
            var Q3;
            Q3=makeQuery(id+"F1.opExtrude","SWEPT_EDGE",EDGE,{"disambiguationData":[OSD([sQuery(id+"F0.wireOp",EDGE,"E15.MirrorCS"),sQuery(id+"F0.wireOp",EDGE,"E16.MirrorCS")])]});
            var Q4;
            Q4=makeQuery(id+"F1.opExtrude","SWEPT_EDGE",EDGE,{"disambiguationData":[OSD([sQuery(id+"F0.wireOp",EDGE,"E9.0"),sQuery(id+"F0.wireOp",EDGE,"E10")])]});
            var Q5;
            Q5=makeQuery(id+"F1.opExtrude","SWEPT_EDGE",EDGE,{"disambiguationData":[OSD([sQuery(id+"F0.wireOp",EDGE,"E8.0"),sQuery(id+"F0.wireOp",EDGE,"E10")])]});
            var Q6;
            Q6=makeQuery(id+"F1.opExtrude","SWEPT_EDGE",EDGE,{"disambiguationData":[OSD([sQuery(id+"F0.wireOp",EDGE,"E11.1.0"),sQuery(id+"F0.wireOp",EDGE,"E11.1.1")])]});
            var Q7;
            Q7=makeQuery(id+"F1.opExtrude","SWEPT_EDGE",EDGE,{"disambiguationData":[OSD([sQuery(id+"F0.wireOp",EDGE,"E11.1.0"),sQuery(id+"F0.wireOp",EDGE,"E11.1.2")])]});
            var Q8;
            Q8=makeQuery(id+"F1.opExtrude","SWEPT_EDGE",EDGE,{"disambiguationData":[OSD([sQuery(id+"F0.wireOp",EDGE,"E11.2.0"),sQuery(id+"F0.wireOp",EDGE,"E11.2.1")])]});
            var Q9;
            Q9=makeQuery(id+"F5.opFillet","BLEND_EDGE",EDGE,{"blendedFrom":[makeQuery(id+"F1.opExtrude","SWEPT_EDGE",EDGE,{"disambiguationData":[OSD([sQuery(id+"F0.wireOp",EDGE,"E11.2.2"),sQuery(id+"F0.wireOp",EDGE,"E42.trimOffspring")])]}),makeQuery(id+"F1.opExtrude","SWEPT_FACE",FACE,{"disambiguationData":[OSD([sQuery(id+"F0.wireOp",EDGE,"E11.2.0")])]})],"blendedInto":[makeQuery(id+"F1.opExtrude","SWEPT_FACE",FACE,{"disambiguationData":[OSD([sQuery(id+"F0.wireOp",EDGE,"E11.2.0")])]})]});
            var Q10;
            Q10=makeQuery(id+"F5.opFillet","BLEND_EDGE",EDGE,{"blendedFrom":[makeQuery(id+"F1.opExtrude","SWEPT_EDGE",EDGE,{"disambiguationData":[OSD([sQuery(id+"F0.wireOp",EDGE,"E23.1.25"),sQuery(id+"F0.wireOp",EDGE,"E29.trimOffspring")])]}),makeQuery(id+"F1.opExtrude","SWEPT_FACE",FACE,{"disambiguationData":[OSD([sQuery(id+"F0.wireOp",EDGE,"E23.1.11")])]})],"blendedInto":[makeQuery(id+"F1.opExtrude","SWEPT_FACE",FACE,{"disambiguationData":[OSD([sQuery(id+"F0.wireOp",EDGE,"E23.1.11")])]})]});
            var Q11;
            Q11=makeQuery(id+"F1.opExtrude","SWEPT_EDGE",EDGE,{"disambiguationData":[OSD([sQuery(id+"F0.wireOp",EDGE,"E23.1.11"),sQuery(id+"F0.wireOp",EDGE,"E23.1.28")])]});
            var Q12;
            Q12=makeQuery(id+"F1.opExtrude","SWEPT_EDGE",EDGE,{"disambiguationData":[OSD([sQuery(id+"F0.wireOp",EDGE,"E23.1.12"),sQuery(id+"F0.wireOp",EDGE,"E23.1.19")])]});
            var Q13;
            Q13=makeQuery(id+"F1.opExtrude","SWEPT_EDGE",EDGE,{"disambiguationData":[OSD([sQuery(id+"F0.wireOp",EDGE,"E23.1.19"),sQuery(id+"F0.wireOp",EDGE,"E23.1.20")])]});
            var Q14;
            Q14=makeQuery(id+"F1.opExtrude","SWEPT_EDGE",EDGE,{"disambiguationData":[OSD([sQuery(id+"F0.wireOp",EDGE,"E23.1.16"),sQuery(id+"F0.wireOp",EDGE,"E23.1.17")])]});
            var Q15;
            Q15=makeQuery(id+"F1.opExtrude","SWEPT_EDGE",EDGE,{"disambiguationData":[OSD([sQuery(id+"F0.wireOp",EDGE,"E23.1.17"),sQuery(id+"F0.wireOp",EDGE,"E23.1.18")])]});
            var Q16;
            Q16=makeQuery(id+"F1.opExtrude","SWEPT_EDGE",EDGE,{"disambiguationData":[OSD([sQuery(id+"F0.wireOp",EDGE,"E23.1.14"),sQuery(id+"F0.wireOp",EDGE,"E23.1.24")])]});
            var Q17;
            Q17=makeQuery(id+"F1.opExtrude","SWEPT_EDGE",EDGE,{"disambiguationData":[OSD([sQuery(id+"F0.wireOp",EDGE,"E23.1.9"),sQuery(id+"F0.wireOp",EDGE,"E23.1.14")])]});
            var Q18;
            Q18=makeQuery(id+"F1.opExtrude","SWEPT_EDGE",EDGE,{"disambiguationData":[OSD([sQuery(id+"F0.wireOp",EDGE,"E23.1.23"),sQuery(id+"F0.wireOp",EDGE,"E23.1.27")])]});
            var Q19;
            Q19=makeQuery(id+"F5.opFillet","BLEND_EDGE",EDGE,{"blendedFrom":[makeQuery(id+"F1.opExtrude","SWEPT_EDGE",EDGE,{"disambiguationData":[OSD([sQuery(id+"F0.wireOp",EDGE,"E23.1.4"),sQuery(id+"F0.wireOp",EDGE,"E23.1.10")])]}),makeQuery(id+"F1.opExtrude","SWEPT_FACE",FACE,{"disambiguationData":[OSD([sQuery(id+"F0.wireOp",EDGE,"E23.1.23")])]})],"blendedInto":[makeQuery(id+"F1.opExtrude","SWEPT_FACE",FACE,{"disambiguationData":[OSD([sQuery(id+"F0.wireOp",EDGE,"E23.1.23")])]})]});
            var Q20;
            Q20=makeQuery(id+"F5.opFillet","BLEND_EDGE",EDGE,{"blendedFrom":[makeQuery(id+"F1.opExtrude","SWEPT_EDGE",EDGE,{"disambiguationData":[OSD([sQuery(id+"F0.wireOp",EDGE,"E23.2.25"),sQuery(id+"F0.wireOp",EDGE,"E46.trimOffspring")])]}),makeQuery(id+"F1.opExtrude","SWEPT_FACE",FACE,{"disambiguationData":[OSD([sQuery(id+"F0.wireOp",EDGE,"E23.2.11")])]})],"blendedInto":[makeQuery(id+"F1.opExtrude","SWEPT_FACE",FACE,{"disambiguationData":[OSD([sQuery(id+"F0.wireOp",EDGE,"E23.2.11")])]})]});
            var Q21;
            Q21=makeQuery(id+"F1.opExtrude","SWEPT_EDGE",EDGE,{"disambiguationData":[OSD([sQuery(id+"F0.wireOp",EDGE,"E23.2.11"),sQuery(id+"F0.wireOp",EDGE,"E23.2.28")])]});
            var Q22;
            Q22=makeQuery(id+"F1.opExtrude","SWEPT_EDGE",EDGE,{"disambiguationData":[OSD([sQuery(id+"F0.wireOp",EDGE,"E23.2.12"),sQuery(id+"F0.wireOp",EDGE,"E23.2.19")])]});
            var Q23;
            Q23=makeQuery(id+"F1.opExtrude","SWEPT_EDGE",EDGE,{"disambiguationData":[OSD([sQuery(id+"F0.wireOp",EDGE,"E23.2.19"),sQuery(id+"F0.wireOp",EDGE,"E23.2.20")])]});
            var Q24;
            Q24=makeQuery(id+"F1.opExtrude","SWEPT_EDGE",EDGE,{"disambiguationData":[OSD([sQuery(id+"F0.wireOp",EDGE,"E23.2.16"),sQuery(id+"F0.wireOp",EDGE,"E23.2.17")])]});
            var Q25;
            Q25=makeQuery(id+"F1.opExtrude","SWEPT_EDGE",EDGE,{"disambiguationData":[OSD([sQuery(id+"F0.wireOp",EDGE,"E23.2.17"),sQuery(id+"F0.wireOp",EDGE,"E23.2.18")])]});
            var Q26;
            Q26=makeQuery(id+"F1.opExtrude","SWEPT_EDGE",EDGE,{"disambiguationData":[OSD([sQuery(id+"F0.wireOp",EDGE,"E23.2.14"),sQuery(id+"F0.wireOp",EDGE,"E23.2.24")])]});
            var Q27;
            Q27=makeQuery(id+"F1.opExtrude","SWEPT_EDGE",EDGE,{"disambiguationData":[OSD([sQuery(id+"F0.wireOp",EDGE,"E23.2.9"),sQuery(id+"F0.wireOp",EDGE,"E23.2.14")])]});
            var Q28;
            Q28=makeQuery(id+"F1.opExtrude","SWEPT_EDGE",EDGE,{"disambiguationData":[OSD([sQuery(id+"F0.wireOp",EDGE,"E23.2.23"),sQuery(id+"F0.wireOp",EDGE,"E23.2.27")])]});
            var Q29;
            Q29=makeQuery(id+"F5.opFillet","BLEND_EDGE",EDGE,{"blendedFrom":[makeQuery(id+"F1.opExtrude","SWEPT_EDGE",EDGE,{"disambiguationData":[OSD([sQuery(id+"F0.wireOp",EDGE,"E23.2.4"),sQuery(id+"F0.wireOp",EDGE,"E23.2.10")])]}),makeQuery(id+"F1.opExtrude","SWEPT_FACE",FACE,{"disambiguationData":[OSD([sQuery(id+"F0.wireOp",EDGE,"E23.2.23")])]})],"blendedInto":[makeQuery(id+"F1.opExtrude","SWEPT_FACE",FACE,{"disambiguationData":[OSD([sQuery(id+"F0.wireOp",EDGE,"E23.2.23")])]})]});
            fillet(context, id + "F7", {"entities" : qUnion([Q0, Q1, Q2, Q3, Q4, Q5, Q6, Q7, Q8, Q9, Q10, Q11, Q12, Q13, Q14, Q15, Q16, Q17, Q18, Q19, Q20, Q21, Q22, Q23, Q24, Q25, Q26, Q27, Q28, Q29]), "radius" : 1 * mm, "tangentPropagation" : true, "allowEdgeOverflow" : false});
        }
        {
            var Q0;
            Q0=makeQuery(id+"F1.opExtrude","CAP_EDGE",EDGE,{"disambiguationData":[OSD([sQuery(id+"F0.wireOp",EDGE,"E41.1.0")])],"isStart":false});
            var Q1;
            Q1=makeQuery(id+"F1.opExtrude","CAP_EDGE",EDGE,{"disambiguationData":[OSD([sQuery(id+"F0.wireOp",EDGE,"E41.1.0")])],"isStart":true});
            chamfer(context, id + "F8", {"entities" : qUnion([Q0, Q1]), "width" : 1 * mm, "tangentPropagation" : true});
        }
        {
            var Q0;
            Q0=makeQuery(id+"F1.opExtrude","SWEPT_FACE",FACE,{"disambiguationData":[OSD([sQuery(id+"F0.wireOp",EDGE,"E41.1.0")])]});
            var sketch = newSketch(context, id + "F9", { "sketchPlane" : qUnion([Q0])});
            skText(sketch, "E48", { "text": "Maughanster V2.0", "fontName": "NotoSansCJKkr-Bold.otf"});
            skPoint(sketch, "E49", {"position": v(-18.42, 3.8) * mm});
            const initialGuessF9  = {"E48": [-0.01842, 0.0023, 1, 0, 0.003]};
            skSetInitialGuess(sketch, initialGuessF9);
            skSolve(sketch);
        }
        {
            var Q0;
            Q0 = qSketchRegion(id + "F9", true);
            extrude(context, id + "F10", {"entities" : qUnion([Q0]), "operationType" : NewBodyOperationType.REMOVE, "oppositeDirection" : true, "depth" : .75 * mm});
        }
    });
